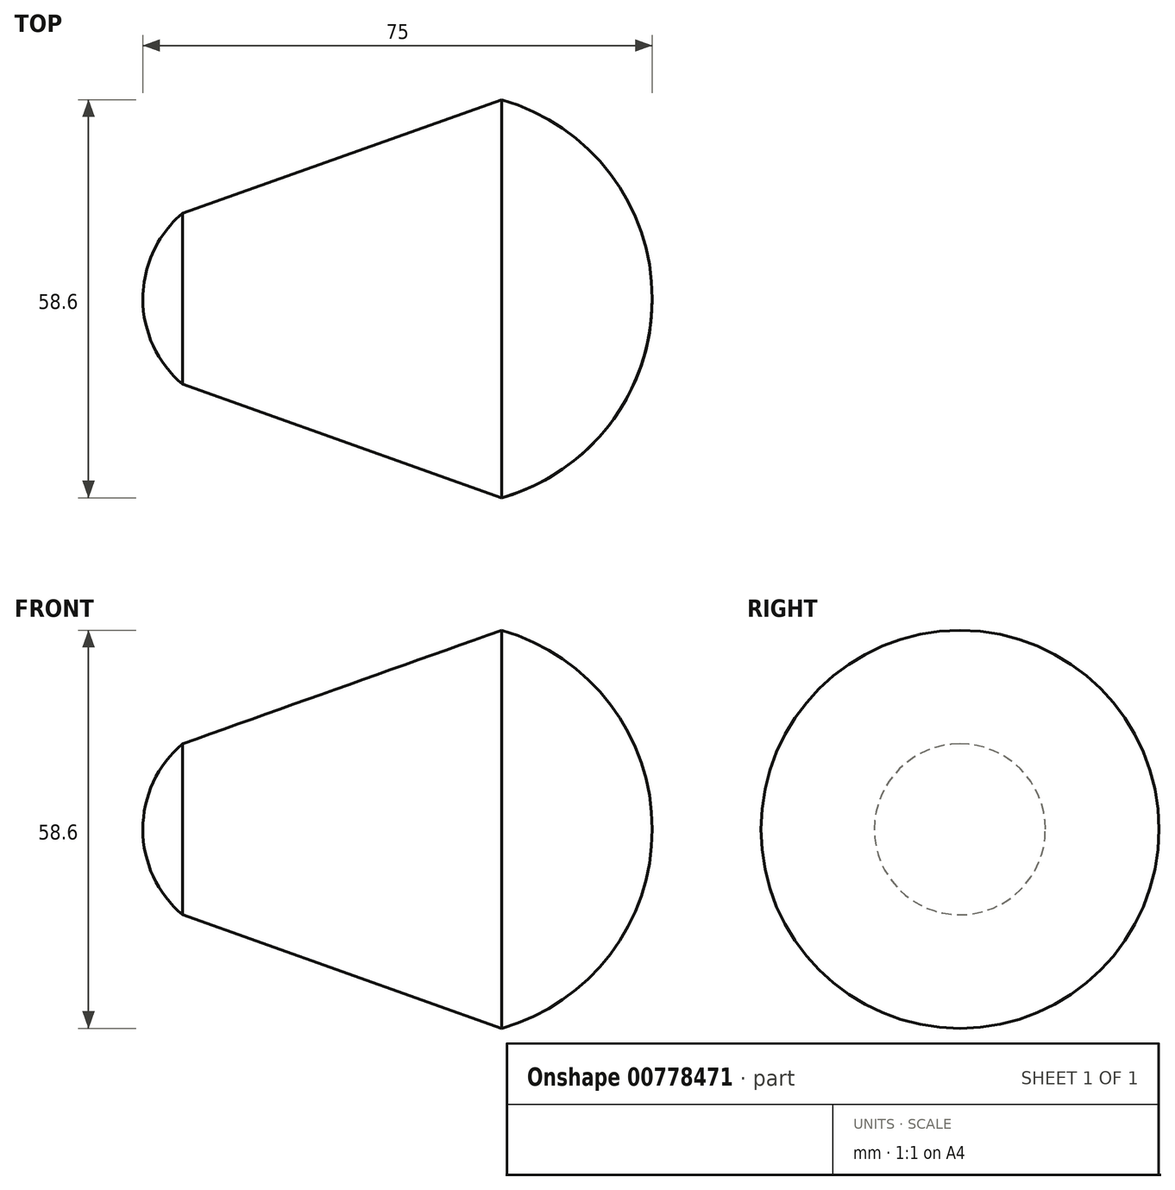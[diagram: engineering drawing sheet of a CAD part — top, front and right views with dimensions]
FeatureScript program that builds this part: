
annotation { "Feature Type Name" : "Feature", "Feature Type Description" : "" }
export const myFeature = defineFeature(function(context is Context, id is Id, definition is map)
    precondition{}
    {
        {
            var Q0;
            Q0=qCreatedBy(makeId("Top.planeOp"),FACE);
            var sketch = newSketch(context, id + "F0", { "sketchPlane" : qUnion([Q0])});
            skLineSegment(sketch, "E0", {"start": v(-36.1, 0) * mm, "end": v(38.9, 0) * mm});
            skArc(sketch, "E1", {"start": v(16.71, 29.3) * mm, "mid": v(32.72, 18.37) * mm, "end": v(38.9, 0) * mm});
            skArc(sketch, "E2", {"start": v(-36.1, 0) * mm, "mid": v(-34.58, 6.93) * mm, "end": v(-30.28, 12.59) * mm});
            skLineSegment(sketch, "E3", {"start": v(-30.28, 12.59) * mm, "end": v(16.71, 29.3) * mm});
            skSolve(sketch);
        }
        {
            var Q0;
            Q0 = qSketchRegion(id + "F0", true);
            var Q1;
            Q1=sQuery(id+"F0.wireOp",EDGE,"E0");
            revolve(context, id + "F1", {"surfaceOperationType" : NewSurfaceOperationType.NEW, "entities" : qUnion([Q0]), "axis" : qUnion([Q1]), "revolveType" : RevolveType.FULL});
        }
    });
